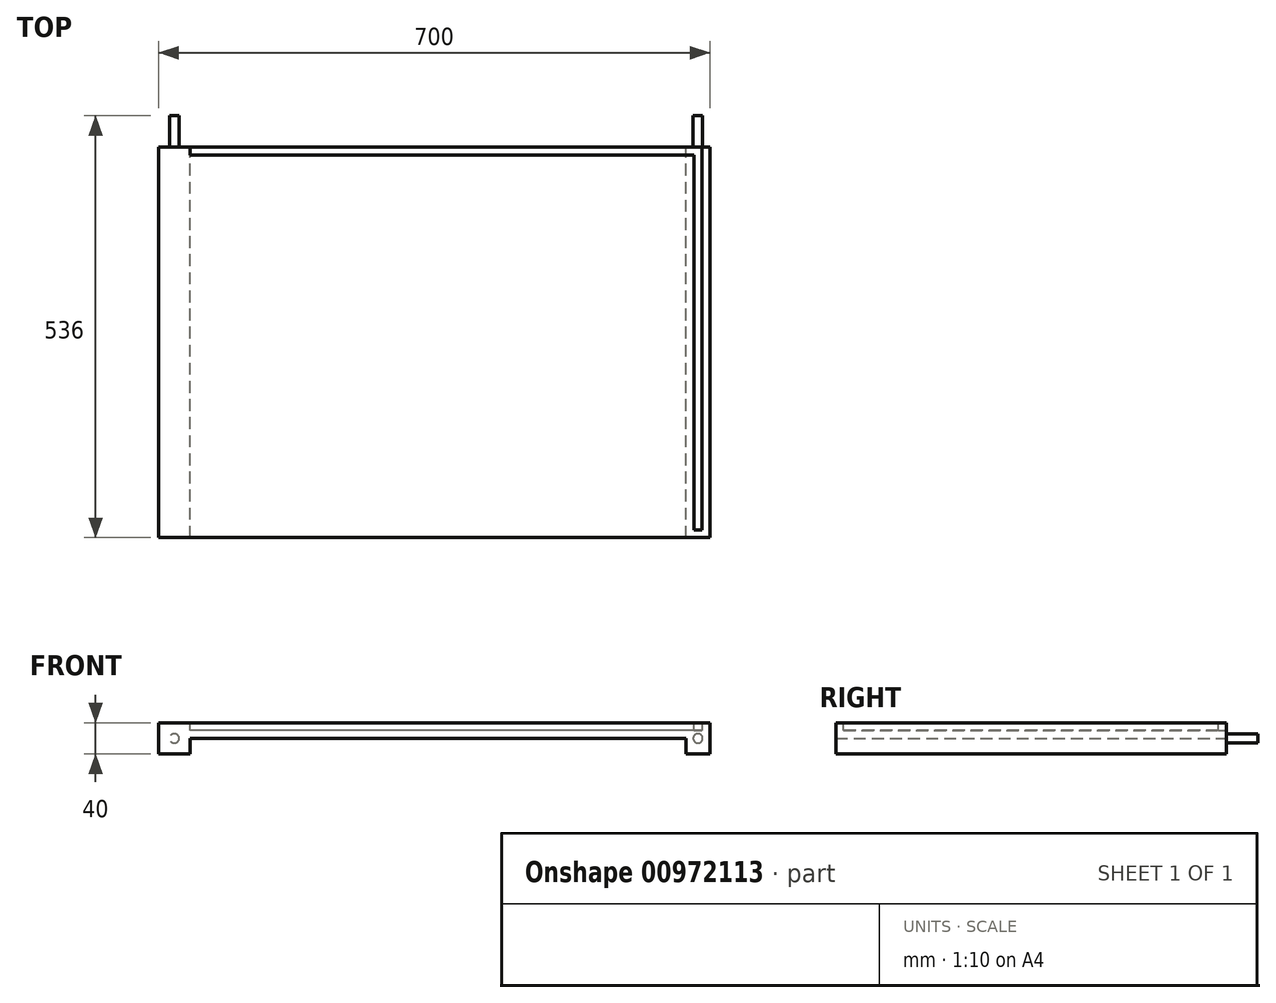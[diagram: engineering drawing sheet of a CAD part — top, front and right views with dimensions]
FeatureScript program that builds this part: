
annotation { "Feature Type Name" : "Feature", "Feature Type Description" : "" }
export const myFeature = defineFeature(function(context is Context, id is Id, definition is map)
    precondition{}
    {
        {
            var Q0;
            Q0=qCreatedBy(makeId("Front.planeOp"),FACE);
            var sketch = newSketch(context, id + "F0", { "sketchPlane" : qUnion([Q0])});
            skLineSegment(sketch, "E0", {"start": v(-325.76, 0) * mm, "end": v(374.24, 0) * mm});
            skLineSegment(sketch, "E1", {"start": v(374.24, 0) * mm, "end": v(374.24, -40) * mm});
            skLineSegment(sketch, "E2", {"start": v(374.24, -40) * mm, "end": v(344.24, -40) * mm});
            skLineSegment(sketch, "E3", {"start": v(344.24, -40) * mm, "end": v(344.24, -20) * mm});
            skLineSegment(sketch, "E4", {"start": v(344.24, -20) * mm, "end": v(-285.76, -20) * mm});
            skLineSegment(sketch, "E5", {"start": v(-285.76, -20) * mm, "end": v(-285.76, -40) * mm});
            skLineSegment(sketch, "E6", {"start": v(-285.76, -40) * mm, "end": v(-325.76, -40) * mm});
            skLineSegment(sketch, "E7", {"start": v(-325.76, 0) * mm, "end": v(-325.76, -40) * mm});
            skSolve(sketch);
        }
        {
            var Q0;
            Q0 = qSketchRegion(id + "F0", true);
            extrude(context, id + "F1", {"entities" : qUnion([Q0]), "depth" : 496 * mm, "offsetDistance" : 25 * mm});
        }
        {
            var Q0;
            Q0=makeQuery(id+"F1.opExtrude","CAP_FACE",FACE,{"disambiguationData":[OSD([sQuery(id+"F0.wireOp",EDGE,"E0"),sQuery(id+"F0.wireOp",EDGE,"E1"),sQuery(id+"F0.wireOp",EDGE,"E2"),sQuery(id+"F0.wireOp",EDGE,"E3"),sQuery(id+"F0.wireOp",EDGE,"E4"),sQuery(id+"F0.wireOp",EDGE,"E5"),sQuery(id+"F0.wireOp",EDGE,"E6"),sQuery(id+"F0.wireOp",EDGE,"E7")])],"isStart":true});
            var sketch = newSketch(context, id + "F2", { "sketchPlane" : qUnion([Q0])});
            skCircle(sketch, "E8", {"center": v(305.76, -20) * mm, "radius": 6 * mm});
            skCircle(sketch, "E9", {"center": v(-359.24, -20) * mm, "radius": 6 * mm});
            skPoint(sketch, "E9.centerSnap0", {"position": v(-374.24, -20) * mm});
            skSolve(sketch);
        }
        {
            var Q0;
            Q0=makeQuery(id+"F2.imprint","IMPRINT",FACE,{"disambiguationData":[TD([[makeQuery(id+"F2.imprint","IMPRINT",EDGE,{"derivedFrom":sQuery(id+"F2.wireOp",EDGE,"E9")}),1.0]])]});
            var Q1;
            Q1=makeQuery(id+"F2.imprint","IMPRINT",FACE,{"disambiguationData":[TD([[makeQuery(id+"F2.imprint","IMPRINT",EDGE,{"derivedFrom":sQuery(id+"F2.wireOp",EDGE,"E8")}),1.0]])]});
            extrude(context, id + "F3", {"entities" : qUnion([Q0, Q1]), "operationType" : NewBodyOperationType.ADD, "depth" : 40 * mm, "offsetDistance" : 25 * mm});
        }
        {
            var Q0;
            Q0=makeQuery(id+"F1.opExtrude","CAP_FACE",FACE,{"disambiguationData":[OSD([sQuery(id+"F0.wireOp",EDGE,"E0"),sQuery(id+"F0.wireOp",EDGE,"E1"),sQuery(id+"F0.wireOp",EDGE,"E2"),sQuery(id+"F0.wireOp",EDGE,"E3"),sQuery(id+"F0.wireOp",EDGE,"E4"),sQuery(id+"F0.wireOp",EDGE,"E5"),sQuery(id+"F0.wireOp",EDGE,"E6"),sQuery(id+"F0.wireOp",EDGE,"E7")])],"isStart":true});
            var Q1;
            Q1=makeQuery(id+"F1.opExtrude","CAP_FACE",FACE,{"disambiguationData":[OSD([sQuery(id+"F0.wireOp",EDGE,"E0"),sQuery(id+"F0.wireOp",EDGE,"E1"),sQuery(id+"F0.wireOp",EDGE,"E2"),sQuery(id+"F0.wireOp",EDGE,"E3"),sQuery(id+"F0.wireOp",EDGE,"E4"),sQuery(id+"F0.wireOp",EDGE,"E5"),sQuery(id+"F0.wireOp",EDGE,"E6"),sQuery(id+"F0.wireOp",EDGE,"E7")])],"isStart":false});
            cPlane(context, id + "F4", {"entities" : qUnion([Q0, Q1]), "cplaneType" : CPlaneType.MID_PLANE, "offset" : 25 * mm, "width" : 150 * mm, "height" : 150 * mm});
        }
        {
            var Q0;
            Q0=makeQuery(id+"F1.opExtrude","CAP_FACE",FACE,{"disambiguationData":[OSD([sQuery(id+"F0.wireOp",EDGE,"E0"),sQuery(id+"F0.wireOp",EDGE,"E1"),sQuery(id+"F0.wireOp",EDGE,"E2"),sQuery(id+"F0.wireOp",EDGE,"E3"),sQuery(id+"F0.wireOp",EDGE,"E4"),sQuery(id+"F0.wireOp",EDGE,"E5"),sQuery(id+"F0.wireOp",EDGE,"E6"),sQuery(id+"F0.wireOp",EDGE,"E7")])],"isStart":true});
            var sketch = newSketch(context, id + "F5", { "sketchPlane" : qUnion([Q0])});
            skLineSegment(sketch, "E10", {"start": v(-364.24, 0) * mm, "end": v(-364.24, -10) * mm});
            skLineSegment(sketch, "E11", {"start": v(-364.24, -10) * mm, "end": v(285.76, -10) * mm});
            skLineSegment(sketch, "E12", {"start": v(285.76, -10) * mm, "end": v(285.76, 0) * mm});
            skLineSegment(sketch, "E13", {"start": v(285.76, 0) * mm, "end": v(-364.24, 0) * mm});
            skSolve(sketch);
        }
        {
            var Q0;
            Q0=makeQuery(id+"F5.imprint","IMPRINT",FACE,{"disambiguationData":[TD([[makeQuery(id+"F5.imprint","IMPRINT",EDGE,{"derivedFrom":sQuery(id+"F5.wireOp",EDGE,"E10")}),1.0]])]});
            extrude(context, id + "F6", {"entities" : qUnion([Q0]), "operationType" : NewBodyOperationType.REMOVE, "oppositeDirection" : true, "depth" : 10 * mm, "offsetDistance" : 25 * mm});
        }
        {
            var Q0;
            Q0=makeQuery(id+"F1.opExtrude","SWEPT_FACE",FACE,{"disambiguationData":[OSD([sQuery(id+"F0.wireOp",EDGE,"E0")])]});
            var sketch = newSketch(context, id + "F7", { "sketchPlane" : qUnion([Q0])});
            skLineSegment(sketch, "E14", {"start": v(364.24, -486) * mm, "end": v(364.24, -10) * mm});
            skLineSegment(sketch, "E15", {"start": v(364.24, -10) * mm, "end": v(354.24, -10) * mm});
            skLineSegment(sketch, "E16", {"start": v(354.24, -10) * mm, "end": v(354.24, -486) * mm});
            skLineSegment(sketch, "E17", {"start": v(354.24, -486) * mm, "end": v(364.24, -486) * mm});
            skSolve(sketch);
        }
        {
            var Q0;
            Q0=makeQuery(id+"F7.imprint","IMPRINT",FACE,{"disambiguationData":[TD([[makeQuery(id+"F7.imprint","IMPRINT",EDGE,{"derivedFrom":sQuery(id+"F7.wireOp",EDGE,"E14")}),1.0]])]});
            extrude(context, id + "F8", {"entities" : qUnion([Q0]), "operationType" : NewBodyOperationType.REMOVE, "oppositeDirection" : true, "depth" : 10 * mm, "offsetDistance" : 25 * mm});
        }
    });
